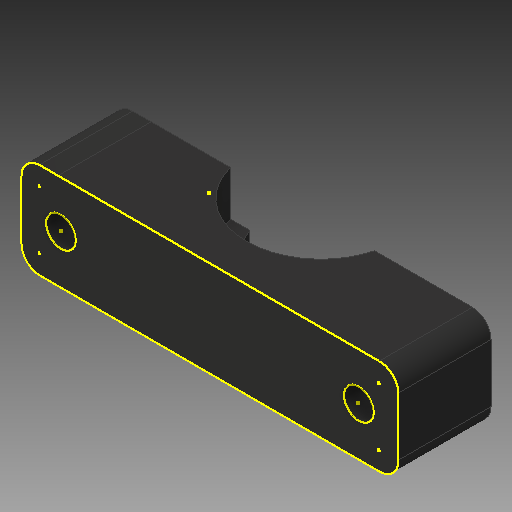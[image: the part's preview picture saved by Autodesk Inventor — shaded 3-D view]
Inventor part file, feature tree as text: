
AUTODESK INVENTOR PART (.ipt)
format: ipt  version: 2018 (Build 220112000, 112)  size: 143,872 bytes
history: native  units: mm
features: sketch x5, other x3
ambient origin geometry x8: Origin, YZ Plane, XZ Plane, XY Plane, X Axis, Y Axis, Z Axis, Center Point
bodies: Solid1 (feature_tree)
feature tree (8):
  other  "Hotend Clamp P1.ipt"
  other  "Solid1::Hotend Clamp P1.ipt"
  other  "TaggingFeature1"
  sketch  "Sketch1"  dims[d0=10.0mm]
  sketch  "Sketch2"
  sketch  "Sketch3"
  sketch  "Sketch4"
  sketch  "Sketch5"
